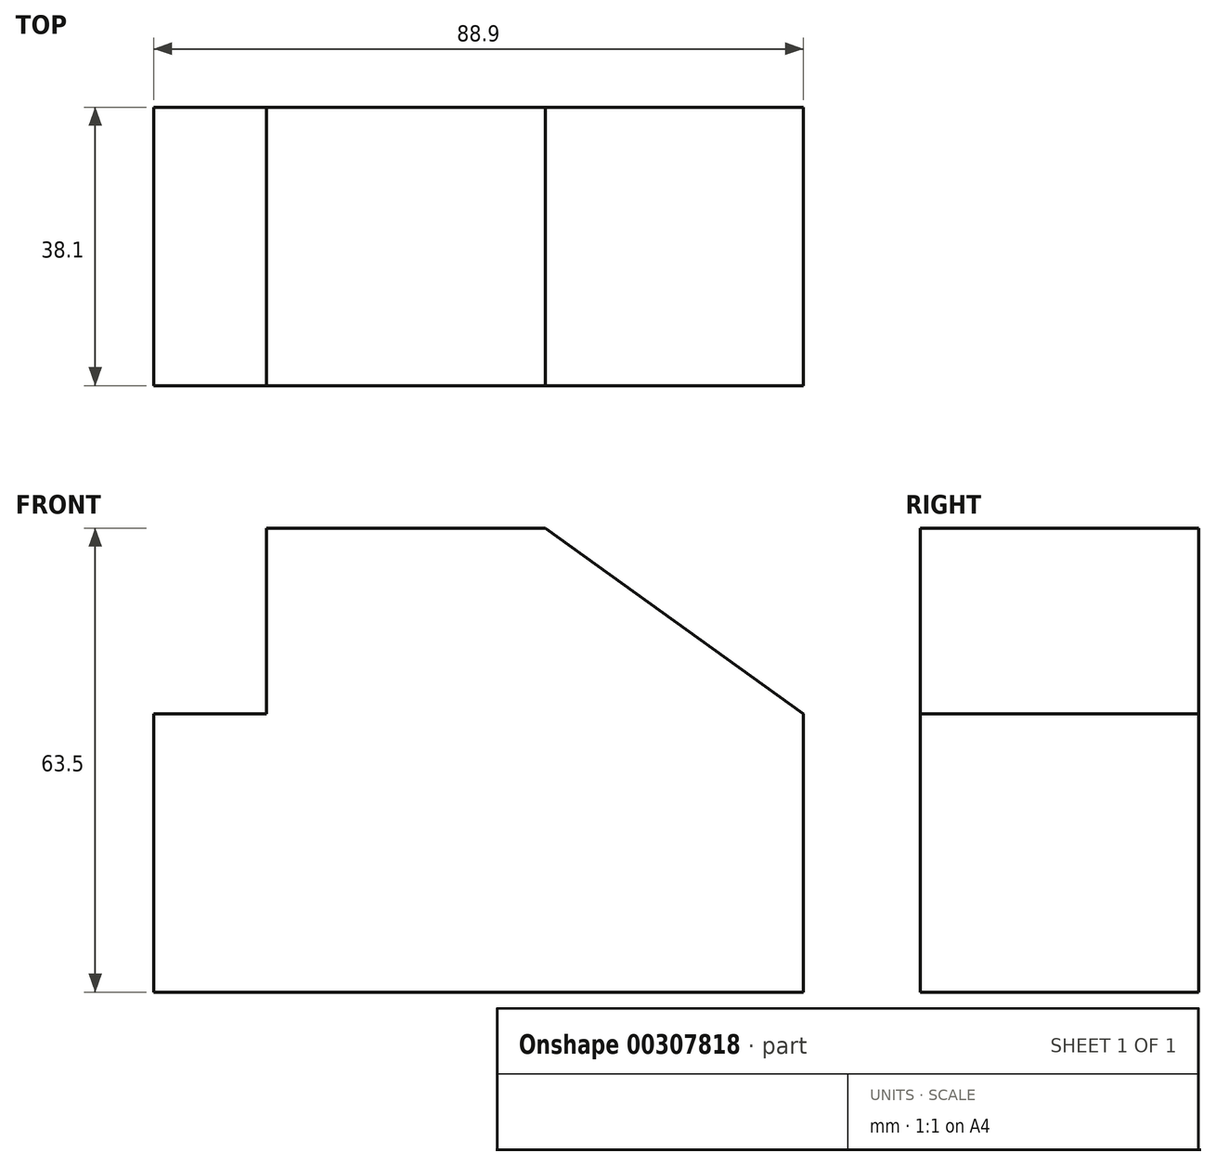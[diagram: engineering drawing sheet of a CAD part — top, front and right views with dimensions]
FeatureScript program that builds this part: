
annotation { "Feature Type Name" : "Feature", "Feature Type Description" : "" }
export const myFeature = defineFeature(function(context is Context, id is Id, definition is map)
    precondition{}
    {
        {
            var Q0;
            Q0=qCreatedBy(makeId("Front.planeOp"),FACE);
            var sketch = newSketch(context, id + "F0", { "sketchPlane" : qUnion([Q0])});
            skLineSegment(sketch, "E0", {"start": v(-38.22, -12.44) * mm, "end": v(50.68, -12.44) * mm});
            skLineSegment(sketch, "E1", {"start": v(50.68, -12.44) * mm, "end": v(50.68, 25.66) * mm});
            skLineSegment(sketch, "E2", {"start": v(-38.22, -12.44) * mm, "end": v(-38.22, 25.66) * mm});
            skLineSegment(sketch, "E3", {"start": v(-38.22, 25.66) * mm, "end": v(-22.76, 25.66) * mm});
            skLineSegment(sketch, "E4", {"start": v(-22.76, 25.66) * mm, "end": v(-22.76, 51.06) * mm});
            skLineSegment(sketch, "E5", {"start": v(-22.76, 51.06) * mm, "end": v(15.34, 51.06) * mm});
            skLineSegment(sketch, "E6", {"start": v(15.34, 51.06) * mm, "end": v(50.68, 25.66) * mm});
            skSolve(sketch);
        }
        {
            var Q0;
            Q0=makeQuery(id+"F0.imprint","IMPRINT",FACE,{"disambiguationData":[TD([[makeQuery(id+"F0.imprint","IMPRINT",EDGE,{"derivedFrom":sQuery(id+"F0.wireOp",EDGE,"E0")}),1.0]])]});
            extrude(context, id + "F1", {"entities" : qUnion([Q0]), "depth" : 38.1 * mm});
        }
    });
